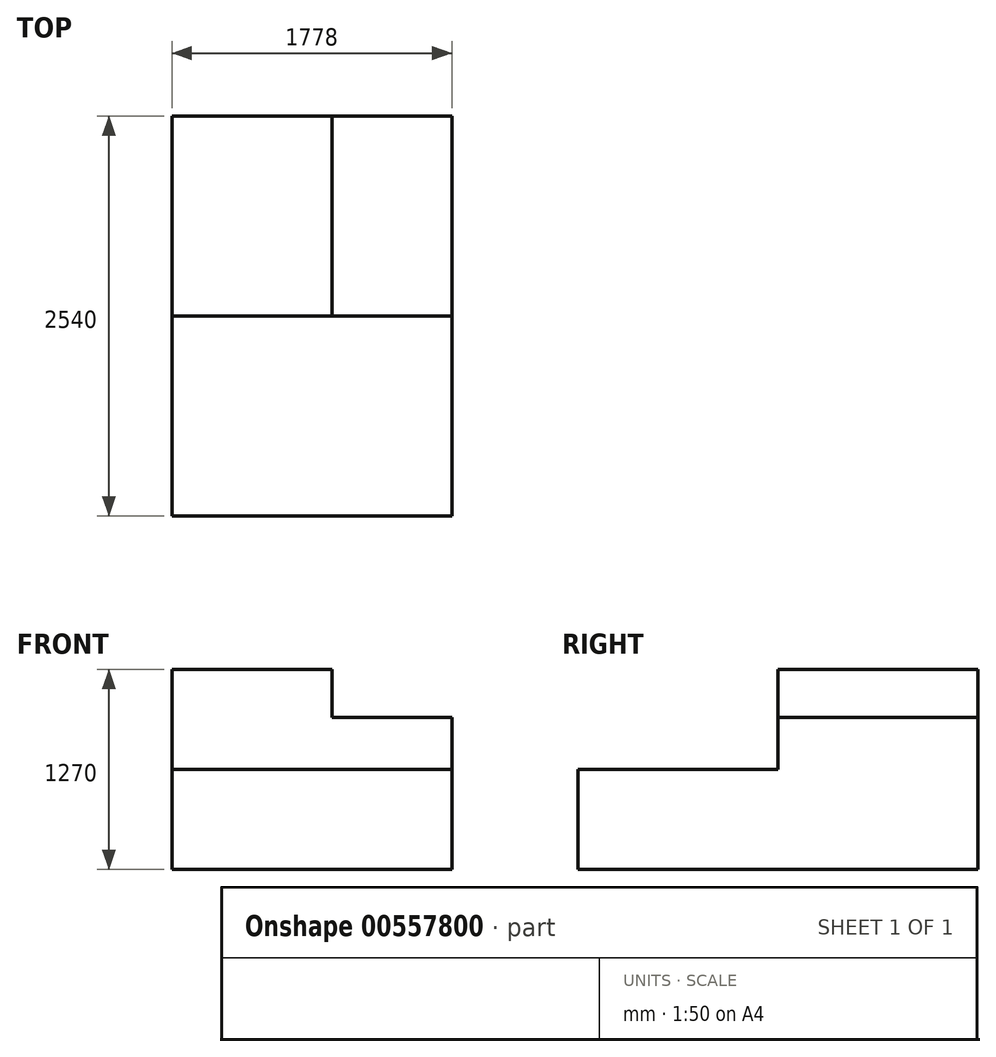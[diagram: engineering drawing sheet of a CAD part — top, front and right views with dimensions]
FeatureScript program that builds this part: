
annotation { "Feature Type Name" : "Feature", "Feature Type Description" : "" }
export const myFeature = defineFeature(function(context is Context, id is Id, definition is map)
    precondition{}
    {
        {
            var Q0;
            Q0=qCreatedBy(makeId("Top.planeOp"),FACE);
            var sketch = newSketch(context, id + "F0", { "sketchPlane" : qUnion([Q0])});
            skLineSegment(sketch, "E0", {"start": v(-66.72, -61.4) * mm, "end": v(1711.28, -61.4) * mm});
            skLineSegment(sketch, "E1", {"start": v(1711.28, -61.4) * mm, "end": v(1711.28, 2478.6) * mm});
            skLineSegment(sketch, "E2", {"start": v(1711.28, 2478.6) * mm, "end": v(-66.72, 2478.6) * mm});
            skLineSegment(sketch, "E3", {"start": v(-66.72, 2478.6) * mm, "end": v(-66.72, -61.4) * mm});
            skLineSegment(sketch, "E4", {"start": v(-66.72, 1208.6) * mm, "end": v(1711.28, 1208.6) * mm});
            skLineSegment(sketch, "E5", {"start": v(949.28, 2478.6) * mm, "end": v(949.28, 1208.6) * mm});
            skSolve(sketch);
        }
        {
            var Q0;
            {var subQ4=sQuery(id+"F0.wireOp",EDGE,"E0");Q0=makeQuery(id+"F0.imprint","IMPRINT",FACE,{"disambiguationData":[TD([[makeQuery(id+"F0.imprint","IMPRINT",EDGE,{"derivedFrom":subQ4}),1.0]])]});}
            extrude(context, id + "F1", {"entities" : qUnion([Q0]), "depth" : 635 * mm, "offsetDistance" : 25.4 * mm});
        }
        {
            var Q0;
            {var subQ5=sQuery(id+"F0.wireOp",EDGE,"E5");Q0=makeQuery(id+"F0.imprint","IMPRINT",FACE,{"disambiguationData":[TD([[makeQuery(id+"F0.imprint","IMPRINT",EDGE,{"derivedFrom":subQ5}),1.0]])]});}
            extrude(context, id + "F2", {"entities" : qUnion([Q0]), "operationType" : NewBodyOperationType.ADD, "depth" : 965.2 * mm, "offsetDistance" : 25.4 * mm});
        }
        {
            var Q0;
            {var subQ3=sQuery(id+"F0.wireOp",EDGE,"E5");Q0=makeQuery(id+"F0.imprint","IMPRINT",FACE,{"disambiguationData":[TD([[makeQuery(id+"F0.imprint","IMPRINT",EDGE,{"derivedFrom":subQ3}),-1.0]])]});}
            extrude(context, id + "F3", {"entities" : qUnion([Q0]), "operationType" : NewBodyOperationType.ADD, "depth" : 1270 * mm, "offsetDistance" : 25.4 * mm});
        }
    });
